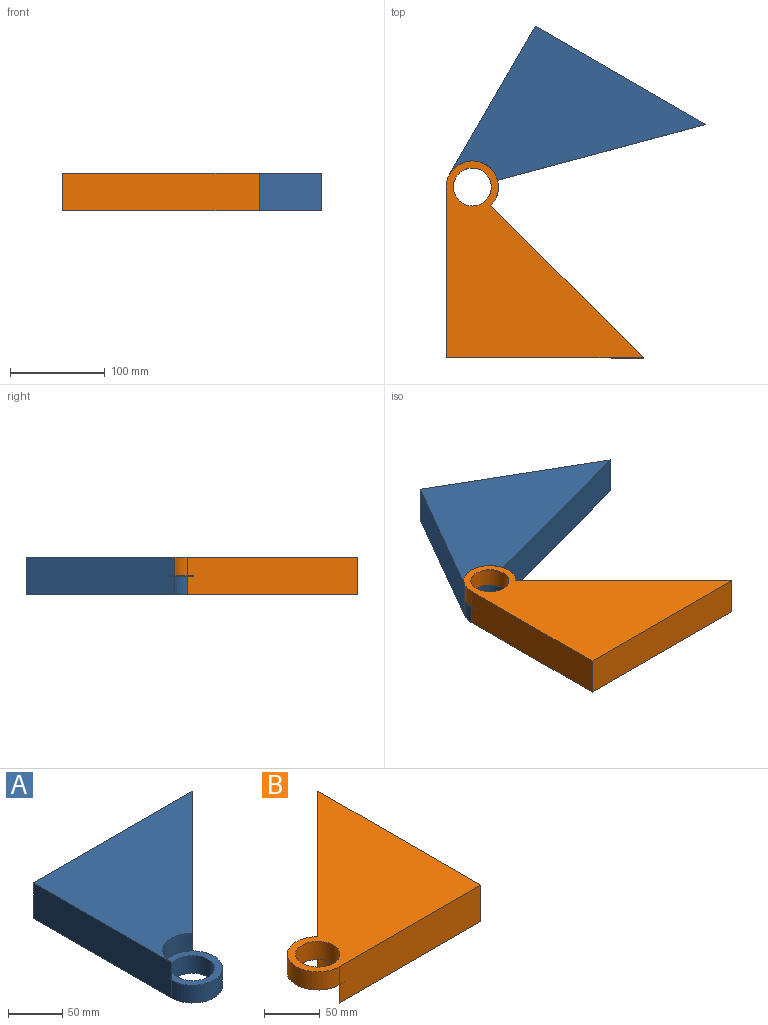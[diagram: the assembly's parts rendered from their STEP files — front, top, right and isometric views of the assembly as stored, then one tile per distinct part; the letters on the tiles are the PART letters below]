
ASSEMBLY  parts=2 mates=1
PART A: 9 faces, bbox 207.5x207.5x40 mm
  f0: cylinder r=27.5mm len=55mm, axis (0,0,-1), area 2159.8mm2, adj f2,f3,f6,f8
  f1: cylinder r=20mm len=40mm, axis (0,0,-1), area 2513.3mm2, adj f6,f8
  f2: plane 180x40mm, normal (-1,0,0), area 7200mm2, adj f0,f4,f5,f6,f7
  f3: plane 160.55x160.55mm, normal (0.71,-0.71,0), area 9082.3mm2, adj f0,f4,f5,f6,f7
  f4: plane 207.5x40mm, normal (0,1,0), area 8300mm2, adj f2,f3,f5,f6
  f5: plane 207.5x180mm, normal (0,0,1), area 20259.1mm2, adj f2,f3,f4,f7
  f6: plane 207.5x207.5mm, normal (0,0,-1), area 21378.3mm2, adj f0,f1,f2,f3,f4
  f7: cylinder r=27.5mm len=46.95mm, axis (0,0,1), area 1295.9mm2, adj f2,f3,f5,f8
  f8: plane 55x55mm, normal (0,0,1), area 1119.2mm2, adj f0,f1,f7
PART B: 9 faces, bbox 207.5x207.5x40 mm
  f0: cylinder r=20mm len=40mm, axis (0,0,-1), area 2513.3mm2, adj f5,f8
  f1: plane 180x40mm, normal (0,-1,0), area 7200mm2, adj f2,f4,f5,f6,f7
  f2: plane 207.5x40mm, normal (1,0,0), area 8300mm2, adj f1,f3,f5,f6
  f3: plane 160.55x160.55mm, normal (-0.71,0.71,0), area 9082.3mm2, adj f2,f4,f5,f6,f7
  f4: cylinder r=27.5mm len=55mm, axis (0,0,-1), area 2159.8mm2, adj f1,f3,f5,f8
  f5: plane 207.5x207.5mm, normal (0,0,1), area 21378.3mm2, adj f0,f1,f2,f3,f4
  f6: plane 207.5x180mm, normal (0,0,-1), area 20259.1mm2, adj f1,f2,f3,f7
  f7: cylinder r=27.5mm len=46.95mm, axis (0,0,-1), area 1295.9mm2, adj f1,f3,f6,f8
  f8: plane 55x55mm, normal (0,0,-1), area 1119.2mm2, adj f0,f4,f7
PLACE A rot(axis=(0,0,-1),30deg) t=(-5.95,266.32,20.37)mm
PLACE B rot(axis=(0,0,-1),90deg) t=(12.99,187.73,20.37)mm
MATE cylindrical B.f0 <-> A.f1  axis (0,0,1) through (-5.95,266.32,60.37)mm
